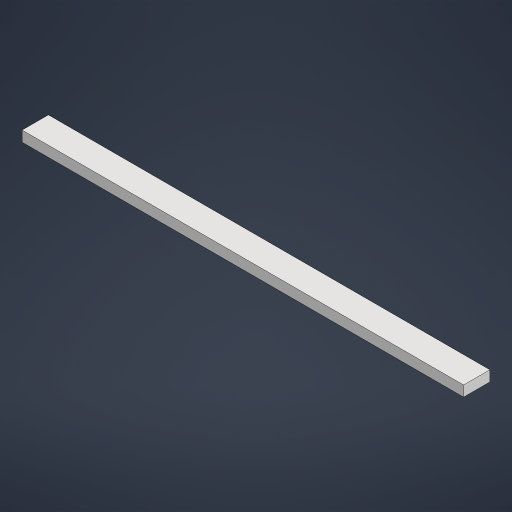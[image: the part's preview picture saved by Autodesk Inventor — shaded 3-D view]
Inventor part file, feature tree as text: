
AUTODESK INVENTOR PART (.ipt)
format: ipt  version: 2023.2 (Build 272271000, 271)  size: 165,888 bytes
history: native  units: in
note: dims shown in document units (in); Inventor stores cm internally (conversion verified against a paired STEP export)
features: extrude x1, sketch x1
ambient origin geometry x8: Origin, YZ Plane, XZ Plane, XY Plane, X Axis, Y Axis, Z Axis, Center Point
bodies: Solid1 (feature_tree)
feature tree (2):
  extrude  "Extrusion1"  Depth=5.0in
  sketch  "Sketch2"  dims[d3=84.0in d4=5.0in d5=2.0in d6=0.0in]
